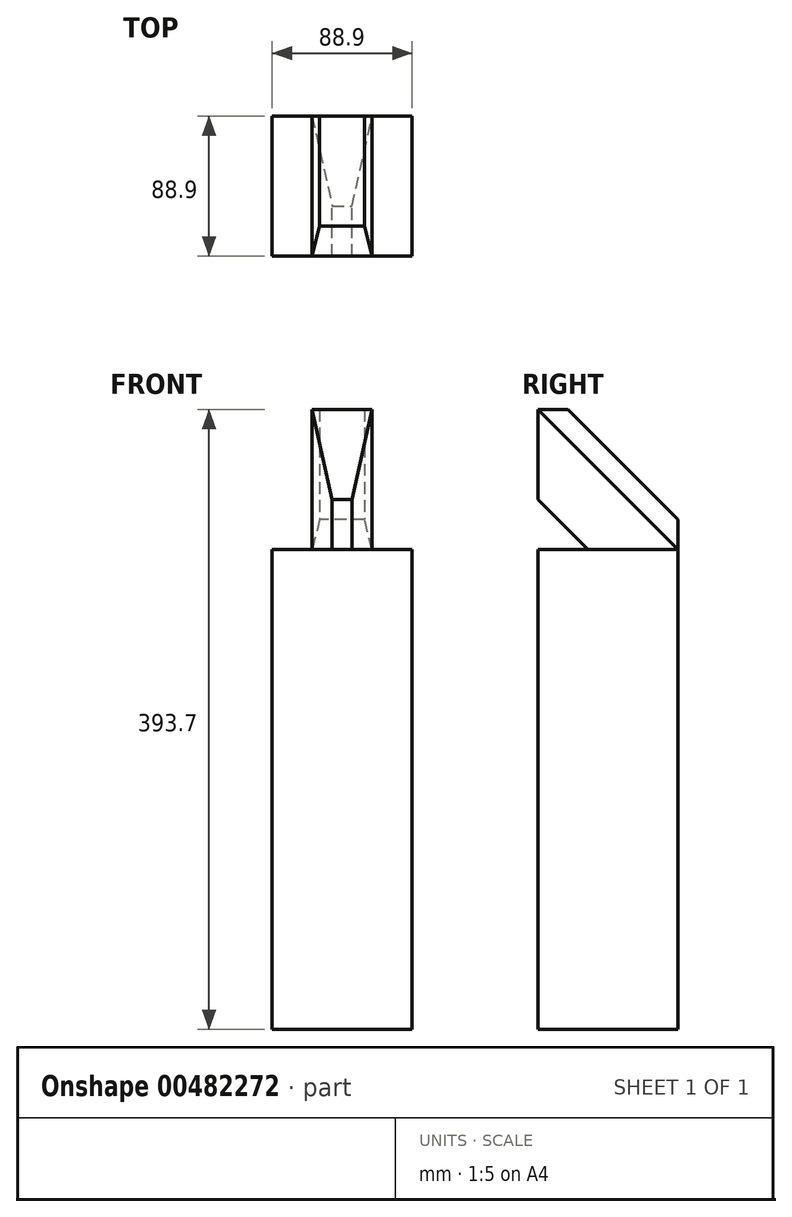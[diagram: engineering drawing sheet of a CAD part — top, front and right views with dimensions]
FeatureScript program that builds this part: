
annotation { "Feature Type Name" : "Feature", "Feature Type Description" : "" }
export const myFeature = defineFeature(function(context is Context, id is Id, definition is map)
    precondition{}
    {
        {
            var Q0;
            Q0=qCreatedBy(makeId("Top.planeOp"),FACE);
            var sketch = newSketch(context, id + "F0", { "sketchPlane" : qUnion([Q0])});
            skLineSegment(sketch, "E0", {"start": v(0, 0) * mm, "end": v(0, -88.9) * mm});
            skLineSegment(sketch, "E1", {"start": v(0, -88.9) * mm, "end": v(88.9, -88.9) * mm});
            skLineSegment(sketch, "E2", {"start": v(88.9, -88.9) * mm, "end": v(88.9, 0) * mm});
            skLineSegment(sketch, "E3", {"start": v(88.9, 0) * mm, "end": v(0, 0) * mm});
            skSolve(sketch);
        }
        {
            var Q0;
            Q0 = qSketchRegion(id + "F0", true);
            extrude(context, id + "F1", {"entities" : qUnion([Q0]), "depth" : 304.8 * mm});
        }
        {
            var Q0;
            Q0=makeQuery(id+"F1.opExtrude","CAP_FACE",FACE,{"disambiguationData":[OSD([sQuery(id+"F0.wireOp",EDGE,"E0"),sQuery(id+"F0.wireOp",EDGE,"E1"),sQuery(id+"F0.wireOp",EDGE,"E2"),sQuery(id+"F0.wireOp",EDGE,"E3")])],"isStart":false});
            var sketch = newSketch(context, id + "F2", { "sketchPlane" : qUnion([Q0])});
            skLineSegment(sketch, "E4", {"start": v(25.43, 0) * mm, "end": v(38.1, -57.15) * mm});
            skLineSegment(sketch, "E5", {"start": v(38.1, -57.15) * mm, "end": v(50.8, -57.15) * mm});
            skLineSegment(sketch, "E6", {"start": v(50.8, -57.15) * mm, "end": v(63.47, 0) * mm});
            skLineSegment(sketch, "E7", {"start": v(63.47, 0) * mm, "end": v(25.43, 0) * mm});
            skLineSegment(sketch, "E8", {"start": v(0, 0) * mm, "end": v(25.43, 0) * mm, "construction": true});
            skLineSegment(sketch, "E9", {"start": v(88.9, 0) * mm, "end": v(63.47, 0) * mm, "construction": true});
            skSolve(sketch);
        }
        {
            var Q0;
            Q0=makeQuery(id+"F1.opExtrude","SWEPT_FACE",FACE,{"disambiguationData":[OSD([sQuery(id+"F0.wireOp",EDGE,"E1")])]});
            var sketch = newSketch(context, id + "F3", { "sketchPlane" : qUnion([Q0])});
            skLineSegment(sketch, "E10", {"start": v(25.43, 393.7) * mm, "end": v(38.1, 336.55) * mm});
            skLineSegment(sketch, "E11", {"start": v(38.1, 336.55) * mm, "end": v(50.8, 336.55) * mm});
            skLineSegment(sketch, "E12", {"start": v(50.8, 336.55) * mm, "end": v(63.47, 393.7) * mm});
            skLineSegment(sketch, "E13", {"start": v(63.47, 393.7) * mm, "end": v(25.43, 393.7) * mm});
            skLineSegment(sketch, "E14", {"start": v(25.43, 393.7) * mm, "end": v(0, 393.7) * mm, "construction": true});
            skLineSegment(sketch, "E15", {"start": v(0, 393.7) * mm, "end": v(0, 304.8) * mm, "construction": true});
            skLineSegment(sketch, "E16", {"start": v(63.47, 393.7) * mm, "end": v(88.9, 393.7) * mm, "construction": true});
            skLineSegment(sketch, "E17", {"start": v(88.9, 393.7) * mm, "end": v(88.9, 304.8) * mm, "construction": true});
            skSolve(sketch);
        }
        {
            var Q1;
            Q1=makeQuery(id+"F3.imprint","IMPRINT",FACE,{"disambiguationData":[TD([[makeQuery(id+"F3.imprint","IMPRINT",EDGE,{"derivedFrom":sQuery(id+"F3.wireOp",EDGE,"E10")}),1.0]])]});
            var Q2;
            Q2=makeQuery(id+"F2.imprint","IMPRINT",FACE,{"disambiguationData":[TD([[makeQuery(id+"F2.imprint","IMPRINT",EDGE,{"derivedFrom":sQuery(id+"F2.wireOp",EDGE,"E4")}),1.0]])]});
            loft(context, id + "F4", {"operationType" : NewBodyOperationType.ADD, "sheetProfilesArray" : [{ "sheetProfileEntities" : qUnion([Q1]) }, { "sheetProfileEntities" : qUnion([Q2]) }]});
        }
        {
            var Q0;
            Q0=makeQuery(id+"F1.opExtrude","SWEPT_FACE",FACE,{"disambiguationData":[OSD([sQuery(id+"F0.wireOp",EDGE,"E3")])]});
            var sketch = newSketch(context, id + "F5", { "sketchPlane" : qUnion([Q0])});
            skLineSegment(sketch, "E18", {"start": v(-63.47, 304.8) * mm, "end": v(-58.74, 323.85) * mm});
            skLineSegment(sketch, "E19", {"start": v(-58.74, 323.85) * mm, "end": v(-30.16, 323.85) * mm});
            skLineSegment(sketch, "E20", {"start": v(-30.16, 323.85) * mm, "end": v(-25.43, 304.8) * mm});
            skLineSegment(sketch, "E21", {"start": v(-25.43, 304.8) * mm, "end": v(-63.47, 304.8) * mm});
            skSolve(sketch);
        }
        {
            var Q0;
            Q0=makeQuery(id+"F1.opExtrude","CAP_FACE",FACE,{"disambiguationData":[OSD([sQuery(id+"F0.wireOp",EDGE,"E0"),sQuery(id+"F0.wireOp",EDGE,"E1"),sQuery(id+"F0.wireOp",EDGE,"E2"),sQuery(id+"F0.wireOp",EDGE,"E3")])],"isStart":false});
            var Q1;
            Q1=makeQuery(id+"F4.opLoft","MID_CAP_VERTEX",VERTEX,{"disambiguationData":[OSD([sQuery(id+"F3.wireOp",EDGE,"E12"),sQuery(id+"F3.wireOp",EDGE,"E13")])],"capPos":0.0});
            cPlane(context, id + "F6", {"entities" : qUnion([Q0, Q1]), "cplaneType" : CPlaneType.PLANE_POINT, "offset" : 25.4 * mm, "width" : 152.4 * mm, "height" : 152.4 * mm});
        }
        {
            var Q0;
            Q0=qCreatedBy(id+"F6.planeOp",FACE);
            var sketch = newSketch(context, id + "F7", { "sketchPlane" : qUnion([Q0])});
            skLineSegment(sketch, "E22", {"start": v(63.47, -88.9) * mm, "end": v(58.74, -69.85) * mm});
            skLineSegment(sketch, "E23", {"start": v(58.74, -69.85) * mm, "end": v(30.16, -69.85) * mm});
            skLineSegment(sketch, "E24", {"start": v(30.16, -69.85) * mm, "end": v(25.43, -88.9) * mm});
            skLineSegment(sketch, "E25", {"start": v(25.43, -88.9) * mm, "end": v(63.47, -88.9) * mm});
            skSolve(sketch);
        }
        {
            var Q1;
            Q1=makeQuery(id+"F7.imprint","IMPRINT",FACE,{"disambiguationData":[TD([[makeQuery(id+"F7.imprint","IMPRINT",EDGE,{"derivedFrom":sQuery(id+"F7.wireOp",EDGE,"E22")}),1.0]])]});
            var Q2;
            Q2=makeQuery(id+"F5.imprint","IMPRINT",FACE,{"disambiguationData":[TD([[makeQuery(id+"F5.imprint","IMPRINT",EDGE,{"derivedFrom":sQuery(id+"F5.wireOp",EDGE,"E18")}),-1.0]])]});
            loft(context, id + "F8", {"operationType" : NewBodyOperationType.ADD, "sheetProfilesArray" : [{ "sheetProfileEntities" : qUnion([Q1]) }, { "sheetProfileEntities" : qUnion([Q2]) }]});
        }
    });
